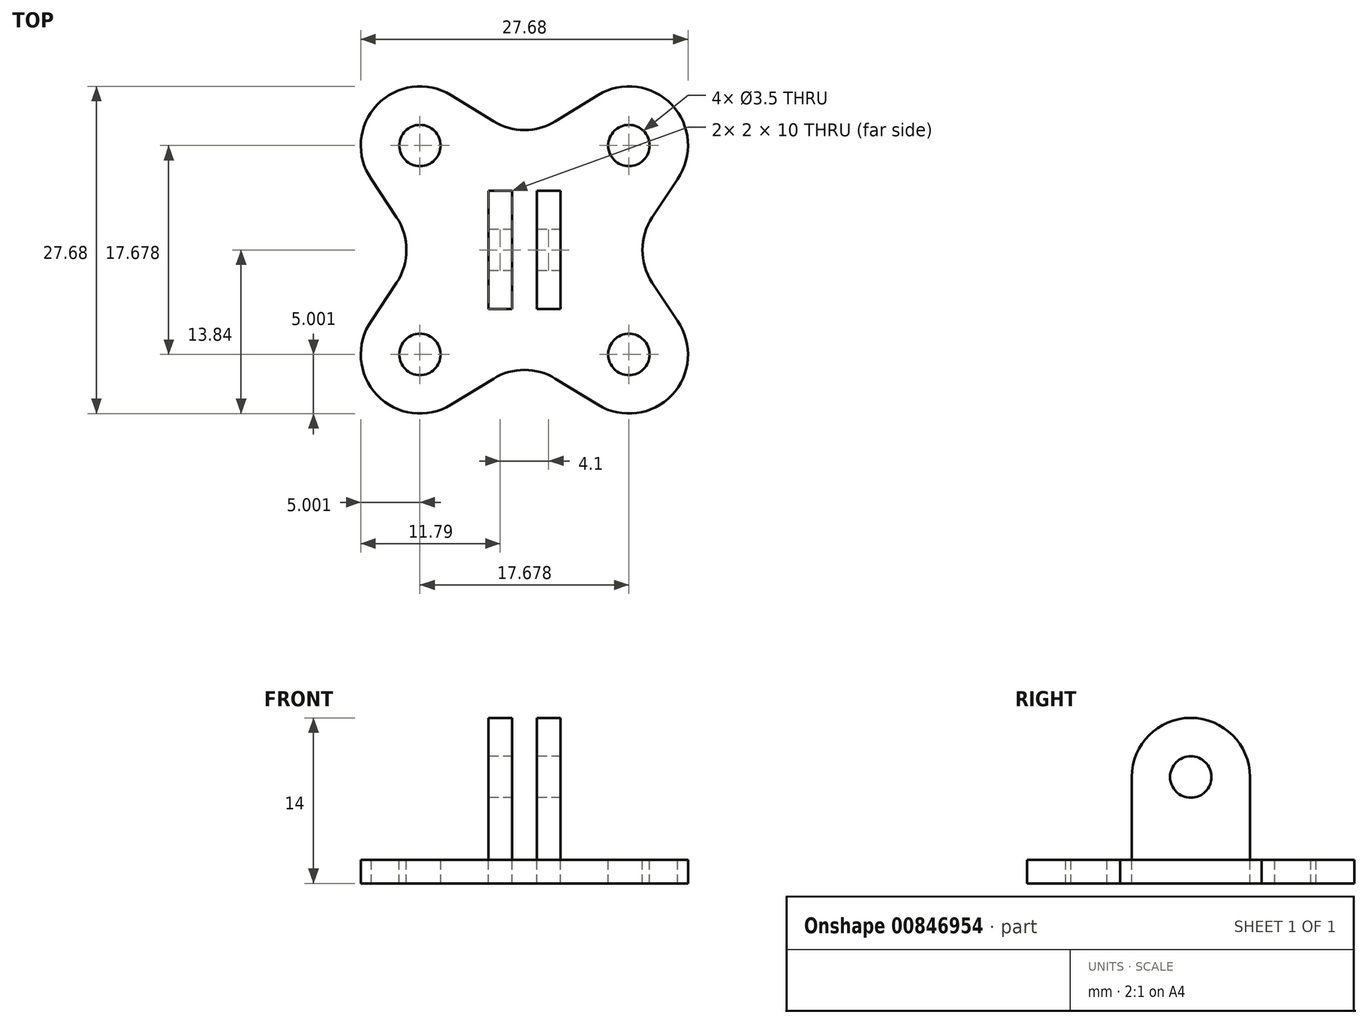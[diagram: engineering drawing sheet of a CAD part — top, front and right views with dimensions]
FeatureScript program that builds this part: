
annotation { "Feature Type Name" : "Feature", "Feature Type Description" : "" }
export const myFeature = defineFeature(function(context is Context, id is Id, definition is map)
    precondition{}
    {
        {
            var Q0;
            Q0=qCreatedBy(makeId("Top.planeOp"),FACE);
            var sketch = newSketch(context, id + "F0", { "sketchPlane" : qUnion([Q0])});
            skLineSegment(sketch, "E0", {"start": v(0, 16.03) * mm, "end": v(0, -20.56) * mm, "construction": true});
            skLineSegment(sketch, "E1", {"start": v(-21.97, 0) * mm, "end": v(21.43, 0) * mm, "construction": true});
            skLineSegment(sketch, "E2", {"start": v(-3.05, 0) * mm, "end": v(-3.05, 5) * mm});
            skLineSegment(sketch, "E3", {"start": v(-3.05, 5) * mm, "end": v(-1.05, 5) * mm});
            skLineSegment(sketch, "E4", {"start": v(-1.05, 5) * mm, "end": v(-1.05, 0) * mm});
            skLineSegment(sketch, "E5.MirrorCS", {"start": v(-3.05, 0) * mm, "end": v(-3.05, -5) * mm});
            skLineSegment(sketch, "E6.MirrorCS", {"start": v(-3.05, -5) * mm, "end": v(-1.05, -5) * mm});
            skLineSegment(sketch, "E7.MirrorCS", {"start": v(-1.05, -5) * mm, "end": v(-1.05, 0) * mm});
            skLineSegment(sketch, "E8.MirrorCS", {"start": v(3.05, 5) * mm, "end": v(1.05, 5) * mm});
            skLineSegment(sketch, "E9.MirrorCS", {"start": v(3.05, 0) * mm, "end": v(3.05, 5) * mm});
            skLineSegment(sketch, "E10.MirrorCS", {"start": v(3.05, 0) * mm, "end": v(3.05, -5) * mm});
            skLineSegment(sketch, "E11.MirrorCS", {"start": v(3.05, -5) * mm, "end": v(1.05, -5) * mm});
            skLineSegment(sketch, "E12.MirrorCS", {"start": v(1.05, -5) * mm, "end": v(1.05, 0) * mm});
            skLineSegment(sketch, "E13.MirrorCS", {"start": v(1.05, 5) * mm, "end": v(1.05, 0) * mm});
            skArc(sketch, "E14", {"start": v(12.95, 6) * mm, "mid": v(12.47, 12.28) * mm, "end": v(6.22, 13.1) * mm});
            skCircle(sketch, "E15", {"center": v(8.84, 8.84) * mm, "radius": 1.75 * mm});
            skLineSegment(sketch, "E16", {"start": v(2.62, 10.89) * mm, "end": v(6.22, 13.1) * mm});
            skLineSegment(sketch, "E17.MirrorCS", {"start": v(10.81, 2.76) * mm, "end": v(12.95, 6) * mm});
            skLineSegment(sketch, "E18.MirrorCS", {"start": v(10.81, -2.76) * mm, "end": v(12.95, -6) * mm});
            skCircle(sketch, "E19.MirrorC", {"center": v(8.84, -8.84) * mm, "radius": 5 * mm});
            skCircle(sketch, "E20.MirrorC", {"center": v(8.84, -8.84) * mm, "radius": 1.75 * mm});
            skLineSegment(sketch, "E21.MirrorCS", {"start": v(2.62, -10.89) * mm, "end": v(6.22, -13.1) * mm});
            skLineSegment(sketch, "E22.MirrorCS", {"start": v(-2.62, 10.89) * mm, "end": v(-6.22, 13.1) * mm});
            skCircle(sketch, "E23.MirrorC", {"center": v(-8.84, 8.84) * mm, "radius": 5 * mm});
            skLineSegment(sketch, "E24.MirrorCS", {"start": v(-10.81, 2.76) * mm, "end": v(-12.95, 6) * mm});
            skLineSegment(sketch, "E25.MirrorCS", {"start": v(-10.81, -2.76) * mm, "end": v(-12.95, -6) * mm});
            skCircle(sketch, "E26.MirrorC", {"center": v(-8.84, -8.84) * mm, "radius": 5 * mm});
            skLineSegment(sketch, "E27.MirrorCS", {"start": v(-2.62, -10.89) * mm, "end": v(-6.22, -13.1) * mm});
            skCircle(sketch, "E28.MirrorC", {"center": v(-8.84, -8.84) * mm, "radius": 1.75 * mm});
            skCircle(sketch, "E29.MirrorC", {"center": v(-8.84, 8.84) * mm, "radius": 1.75 * mm});
            skPoint(sketch, "E30.visualSharp", {"position": v(8.99, 0) * mm});
            skArc(sketch, "E30.filletArc", {"start": v(10.81, 2.76) * mm, "mid": v(9.98, 0) * mm, "end": v(10.81, -2.76) * mm});
            skPoint(sketch, "E31.visualSharp", {"position": v(0, -9.28) * mm});
            skArc(sketch, "E31.filletArc", {"start": v(2.62, -10.89) * mm, "mid": v(0, -10.15) * mm, "end": v(-2.62, -10.89) * mm});
            skPoint(sketch, "E32.visualSharp", {"position": v(-8.99, 0) * mm});
            skArc(sketch, "E32.filletArc", {"start": v(-10.81, -2.76) * mm, "mid": v(-9.98, 0) * mm, "end": v(-10.81, 2.76) * mm});
            skPoint(sketch, "E33.visualSharp", {"position": v(0, 9.28) * mm});
            skArc(sketch, "E33.filletArc", {"start": v(-2.62, 10.89) * mm, "mid": v(0, 10.15) * mm, "end": v(2.62, 10.89) * mm});
            skSolve(sketch);
        }
        {
            var Q0;
            Q0=makeQuery(id+"F0.imprint","IMPRINT",FACE,{"disambiguationData":[TD([[makeQuery(id+"F0.imprint","IMPRINT",EDGE,{"derivedFrom":sQuery(id+"F0.wireOp",EDGE,"E2")}),-1.0]])]});
            var Q1;
            Q1=makeQuery(id+"F0.imprint","IMPRINT",FACE,{"disambiguationData":[TD([[makeQuery(id+"F0.imprint","IMPRINT",EDGE,{"derivedFrom":sQuery(id+"F0.wireOp",EDGE,"E8.MirrorCS")}),1.0]])]});
            extrude(context, id + "F1", {"entities" : qUnion([Q0, Q1]), "depth" : 12 * mm, "offsetDistance" : 25 * mm});
        }
        {
            var Q0;
            Q0=makeQuery(id+"F0.imprint","IMPRINT",FACE,{"disambiguationData":[TD([[makeQuery(id+"F0.imprint","IMPRINT",EDGE,{"derivedFrom":sQuery(id+"F0.wireOp",EDGE,"8rirtNga-VCeB-YCmm-ql7M-FvKKBExAqGDW")}),1.0]])]});
            var Q1;
            Q1=makeQuery(id+"F0.imprint","IMPRINT",FACE,{"disambiguationData":[TD([[makeQuery(id+"F0.imprint","IMPRINT",EDGE,{"derivedFrom":sQuery(id+"F0.wireOp",EDGE,"E2")}),-1.0]])]});
            var Q2;
            Q2=makeQuery(id+"F0.imprint","IMPRINT",FACE,{"disambiguationData":[TD([[makeQuery(id+"F0.imprint","IMPRINT",EDGE,{"derivedFrom":sQuery(id+"F0.wireOp",EDGE,"E8.MirrorCS")}),1.0]])]});
            var Q3;
            {var subQ1=sQuery(id+"F0.wireOp",EDGE,"f6729957-78fc-439c-b0a8-2d52ed6cbd8f0.MirrorCS");Q3=makeQuery(id+"F0.imprint","IMPRINT",FACE,{"disambiguationData":[TD([[makeQuery(id+"F0.imprint","IMPRINT",EDGE,{"derivedFrom":subQ1}),-1.0]])]});}
            var Q4;
            {var subQ0=sQuery(id+"F0.wireOp",EDGE,"70513b72-b72a-4e81-b547-6f4ce594ac1e0.MirrorCS");Q4=makeQuery(id+"F0.imprint","IMPRINT",FACE,{"disambiguationData":[TD([[makeQuery(id+"F0.imprint","IMPRINT",EDGE,{"derivedFrom":subQ0}),-1.0]])]});}
            var Q5;
            {var subQ4=sQuery(id+"F0.wireOp",EDGE,"fcfe764b-df2a-4d67-98b5-248d5cffb6fe0.MirrorCS");Q5=makeQuery(id+"F0.imprint","IMPRINT",FACE,{"disambiguationData":[TD([[makeQuery(id+"F0.imprint","IMPRINT",EDGE,{"derivedFrom":subQ4}),-1.0]])]});}
            var Q6;
            {var subQ6=sQuery(id+"F0.wireOp",EDGE,"lBa4HMik-piy8-FSBF-c2o0-1Cl6q7hAxig7");Q6=makeQuery(id+"F0.imprint","IMPRINT",FACE,{"disambiguationData":[TD([[makeQuery(id+"F0.imprint","IMPRINT",EDGE,{"derivedFrom":subQ6}),1.0]])]});}
            extrude(context, id + "F2", {"entities" : qUnion([Q0, Q1, Q2, Q3, Q4, Q5, Q6]), "depth" : -2 * mm, "offsetDistance" : 25 * mm});
        }
        {
            var Q0;
            Q0=makeQuery(id+"F1.opExtrude","SWEPT_FACE",FACE,{"disambiguationData":[OSD([sQuery(id+"F0.wireOp",EDGE,"E2"),sQuery(id+"F0.wireOp",EDGE,"E5.MirrorCS")])]});
            var sketch = newSketch(context, id + "F3", { "sketchPlane" : qUnion([Q0])});
            skLineSegment(sketch, "E34", {"start": v(0, 12) * mm, "end": v(0, 3.7) * mm, "construction": true});
            skLineSegment(sketch, "E35", {"start": v(-5, 12) * mm, "end": v(5, 12) * mm, "construction": true});
            skLineSegment(sketch, "E36", {"start": v(0, 12) * mm, "end": v(0, 7) * mm, "construction": true});
            skCircle(sketch, "E37", {"center": v(0, 7) * mm, "radius": 5 * mm});
            skCircle(sketch, "E38", {"center": v(0, 7) * mm, "radius": 1.75 * mm});
            skSolve(sketch);
        }
        {
            var Q0;
            {var subQ0=sQuery(id+"F3.wireOp",EDGE,"E37");var subQ1=sQuery(id+"F0.wireOp",EDGE,"E2");var subQ2=makeQuery(id+"F1.opExtrude","CAP_EDGE",EDGE,{"disambiguationData":[OSD([subQ1,sQuery(id+"F0.wireOp",EDGE,"E5.MirrorCS")])],"isStart":false});var subQ3=makeQuery(id+"F3.imprint","INTERSECT",VERTEX,{"derivedFrom":[subQ2,subQ0]});Q0=makeQuery(id+"F3.imprint","IMPRINT",FACE,{"disambiguationData":[TD([[makeQuery(id+"F3.imprint","IMPRINT",EDGE,{"disambiguationData":[TD([[subQ3,-1.0]])],"derivedFrom":subQ0}),-1.0]])]});}
            var Q1;
            Q1=makeQuery(id+"F3.imprint","IMPRINT",FACE,{"disambiguationData":[TD([[makeQuery(id+"F3.imprint","IMPRINT",EDGE,{"derivedFrom":sQuery(id+"F3.wireOp",EDGE,"E38")}),1.0]])]});
            var Q2;
            {var subQ0=sQuery(id+"F3.wireOp",EDGE,"E37");var subQ1=sQuery(id+"F0.wireOp",EDGE,"E5.MirrorCS");var subQ2=makeQuery(id+"F1.opExtrude","CAP_EDGE",EDGE,{"disambiguationData":[OSD([sQuery(id+"F0.wireOp",EDGE,"E2"),subQ1])],"isStart":false});var subQ3=makeQuery(id+"F3.imprint","INTERSECT",VERTEX,{"derivedFrom":[subQ2,subQ0]});Q2=makeQuery(id+"F3.imprint","IMPRINT",FACE,{"disambiguationData":[TD([[makeQuery(id+"F3.imprint","IMPRINT",EDGE,{"disambiguationData":[TD([[subQ3,1.0]])],"derivedFrom":subQ0}),-1.0]])]});}
            extrude(context, id + "F4", {"entities" : qUnion([Q0, Q1, Q2]), "operationType" : NewBodyOperationType.REMOVE, "oppositeDirection" : true, "depth" : 25 * mm, "offsetDistance" : 25 * mm});
        }
        {
            var Q0;
            Q0=qSketchRegion(id+"F0",true);
            extrude(context, id + "F5", {"entities" : qUnion([Q0]), "depth" : -2 * mm, "offsetDistance" : 25 * mm});
        }
    });
